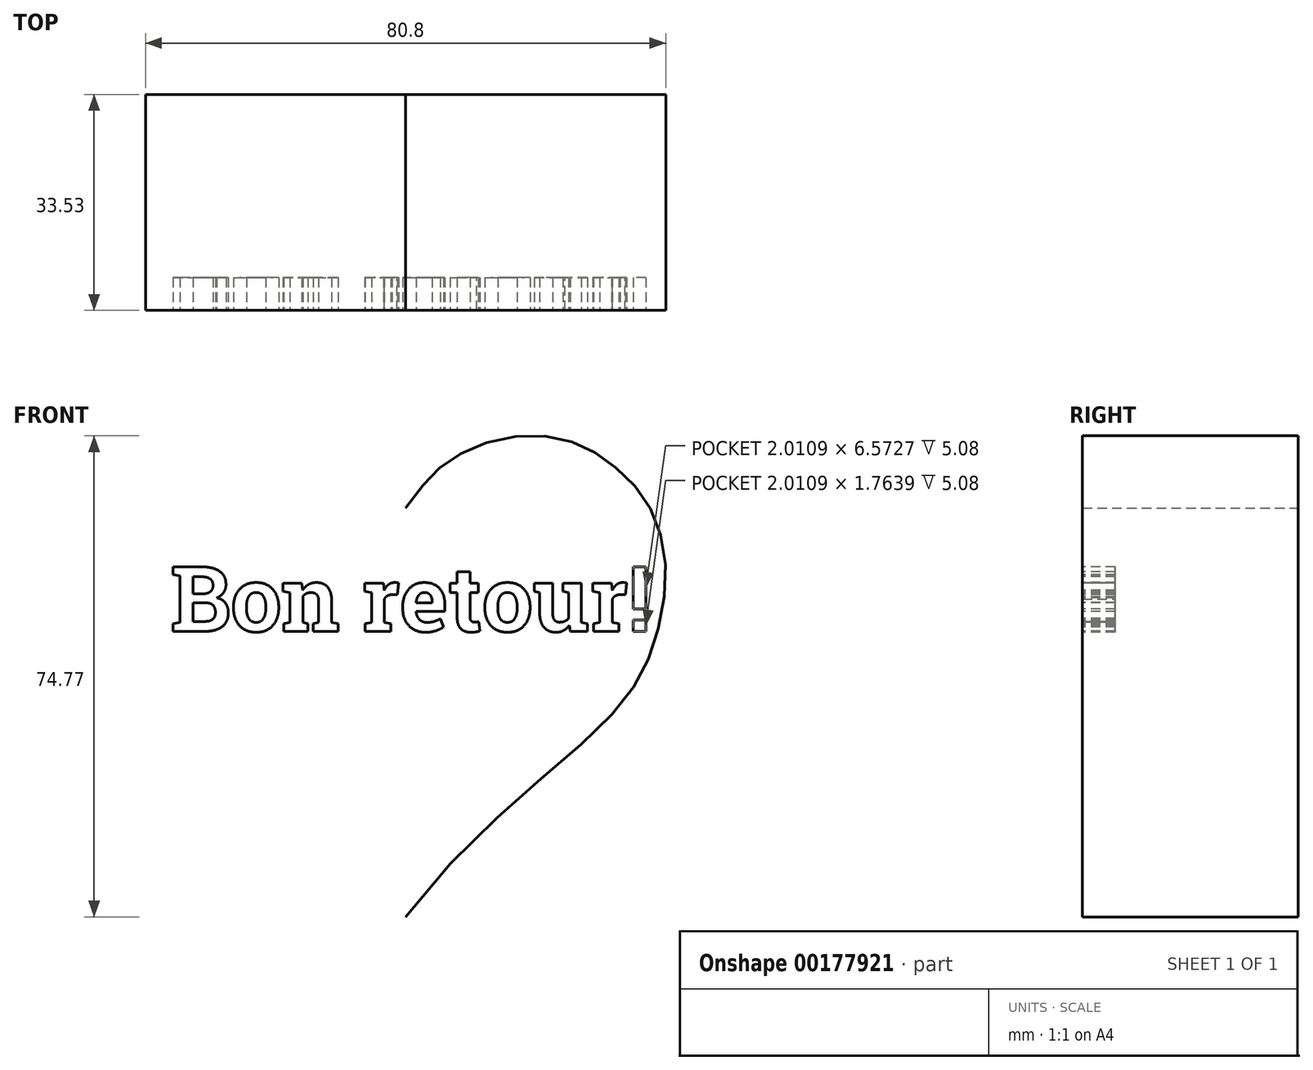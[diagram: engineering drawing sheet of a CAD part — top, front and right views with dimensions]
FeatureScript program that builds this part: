
annotation { "Feature Type Name" : "Feature", "Feature Type Description" : "" }
export const myFeature = defineFeature(function(context is Context, id is Id, definition is map)
    precondition{}
    {
        {
            var Q0;
            Q0=qCreatedBy(makeId("Front.planeOp"),FACE);
            var sketch = newSketch(context, id + "F0", { "sketchPlane" : qUnion([Q0])});
            skFitSpline(sketch, "E0", {"points": [v(0, 13.21) * mm, v(-5.52, 19.6) * mm, v(-13.65, 23.67) * mm, v(-24.1, 23.96) * mm, v(-31.37, 20.47) * mm, v(-37.46, 14.09) * mm, v(-40.37, 4.21) * mm, v(-38.34, -8.57) * mm, v(-30.78, -20.18) * mm, v(0, -50.35) * mm], "startDerivative": vector(-70.8, 96.08) * mm, "endDerivative": vector(154.55, -205.45) * mm});
            skFitSpline(sketch, "E1.MirrorCS", {"points": [v(0, 13.21) * mm, v(5.52, 19.6) * mm, v(13.65, 23.67) * mm, v(24.1, 23.96) * mm, v(31.37, 20.47) * mm, v(37.46, 14.09) * mm, v(40.37, 4.21) * mm, v(38.34, -8.57) * mm, v(30.78, -20.18) * mm, v(0, -50.35) * mm], "startDerivative": vector(70.8, 96.08) * mm, "endDerivative": vector(-154.55, -205.45) * mm});
            skSolve(sketch);
        }
        {
            var Q0;
            Q0=makeQuery(id+"F0.imprint","IMPRINT",FACE,{"disambiguationData":[TD([[makeQuery(id+"F0.imprint","IMPRINT",EDGE,{"derivedFrom":sQuery(id+"F0.wireOp",EDGE,"E0")}),1.0]])]});
            var sketch = newSketch(context, id + "F1", { "sketchPlane" : qUnion([Q0])});
            skSolve(sketch);
        }
        {
            var Q0;
            Q0 = qSketchRegion(id + "F1", true);
            var Q1;
            Q1=makeQuery(id+"F0.imprint","IMPRINT",FACE,{"disambiguationData":[TD([[makeQuery(id+"F0.imprint","IMPRINT",EDGE,{"derivedFrom":sQuery(id+"F0.wireOp",EDGE,"E0")}),1.0]])]});
            extrude(context, id + "F2", {"entities" : qUnion([Q0, Q1]), "depth" : 33.53 * mm});
        }
        {
            var Q0;
            Q0=makeQuery(id+"F2.opExtrude","CAP_FACE",FACE,{"disambiguationData":[OSD([sQuery(id+"F0.wireOp",EDGE,"E0"),sQuery(id+"F0.wireOp",EDGE,"E1.MirrorCS")])],"isStart":false});
            var sketch = newSketch(context, id + "F3", { "sketchPlane" : qUnion([Q0])});
            skText(sketch, "E2", { "text": "Bon retour!", "fontName": "RobotoSlab-Bold.ttf"});
            const initialGuessF3  = {"E2": [-0.03652, -0.00598, 1, 0, 0.01016]};
            skSetInitialGuess(sketch, initialGuessF3);
            skSolve(sketch);
        }
        {
            var Q0;
            Q0 = qSketchRegion(id + "F3", true);
            extrude(context, id + "F4", {"entities" : qUnion([Q0]), "operationType" : NewBodyOperationType.REMOVE, "oppositeDirection" : true, "depth" : 5.08 * mm});
        }
    });
